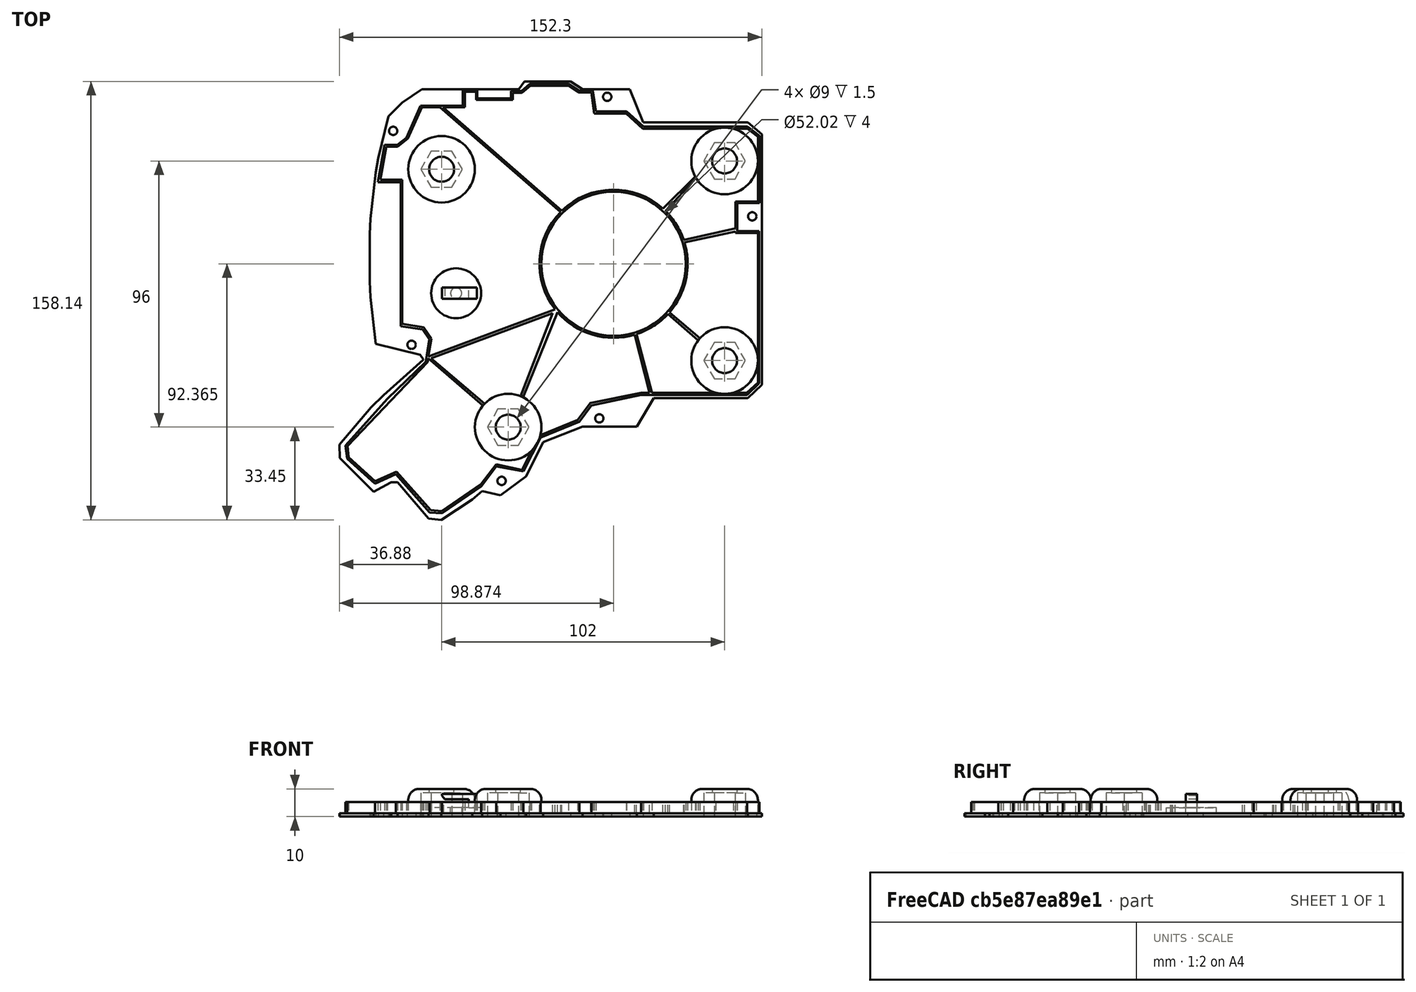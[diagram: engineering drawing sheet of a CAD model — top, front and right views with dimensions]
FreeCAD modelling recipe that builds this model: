
FCSTD DOCUMENT  (FreeCAD 0.19R19127 (Git))
Label: bottom
License: All rights reserved
LicenseURL: http://en.wikipedia.org/wiki/All_rights_reserved
objects: Part::Extrusion×13, Sketcher::SketchObject×9, Part::Cut×7, Part::MultiFuse×2, Mesh::Feature×1, Part::Fillet×1
note: 32 computed .brp shape members not serialized (recipe doc carries the construction recipe); baked Part::Feature solids carry a one-line shape summary decoded from their .brp

FEATURE [Mesh::Feature] Micro_push_button
  Placement = pos=(-31.692,-13.956,0) rot=(0,1,0;3.14159rad)
FEATURE [Sketcher::SketchObject] Sketch
  Placement = pos=(0,0,0) rot=(1,0,0;1.5708rad)
  sketch-geometry (7):
    g0: LineSegment StartX=-27.2326 StartY=-4.41101 StartZ=0 EndX=-27.2326 EndY=-1.0147 EndZ=0
    g1: LineSegment StartX=-27.2326 StartY=-1.0147 StartZ=0 EndX=-35.909 EndY=-1.0147 EndZ=0
    g2: LineSegment StartX=-35.909 StartY=-1.0147 StartZ=0 EndX=-36.8322 EndY=0.249898 EndZ=0
    g3: LineSegment StartX=-36.8322 StartY=0.249898 StartZ=0 EndX=-36.8322 EndY=0.921976 EndZ=0
    g4: LineSegment StartX=-36.8322 StartY=0.921976 StartZ=0 EndX=-24.2326 EndY=0.921976 EndZ=0
    g5: LineSegment StartX=-24.2326 StartY=0.921976 StartZ=0 EndX=-24.2326 EndY=-4.41101 EndZ=0
    g6: LineSegment StartX=-24.2326 StartY=-4.41101 StartZ=0 EndX=-27.2326 EndY=-4.41101 EndZ=0
  constraints (14):
    c: Vertical(g0)
    c: Coincident(g0,g1)
    c: Horizontal(g1)
    c: Coincident(g1,g2)
    c: Coincident(g2,g3)
    c: Vertical(g3)
    c: Coincident(g3,g4)
    c: Horizontal(g4)
    c: Coincident(g4,g5)
    c: Vertical(g5)
    c: Coincident(g6,g5)
    c: Coincident(g6,g0)
    c: Horizontal(g6)
    c: Distance(g6) = 3
FEATURE [Part::Extrusion] Extrude  label="Schalterhalter"
  Base = -> Sketch
  Dir = (0,-1,2e-16)
  DirMode = 2
  FaceMakerClass = Part::FaceMakerBullseye
  LengthFwd = 4
  LengthRev = 0
  Placement = pos=(0,-10.7,0) rot=(0,0,1;0rad)
  Solid = true
  Symmetric = false
FEATURE [Sketcher::SketchObject] Sketch031
  Placement = pos=(0,0,0) rot=(1,0,0;3.14159rad)
  sketch-geometry (93):
    g0: LineSegment StartX=-24.1385 StartY=-60.4779 StartZ=0 EndX=-29.3451 EndY=-60.4779 EndZ=0
    g1: LineSegment StartX=-29.3451 StartY=-60.4779 StartZ=0 EndX=-29.3451 EndY=-54.9411 EndZ=0
    g2: LineSegment StartX=-29.3451 StartY=-54.9411 StartZ=0 EndX=-44.617 EndY=-54.9411 EndZ=0
    g3: LineSegment StartX=-44.617 StartY=-54.9411 StartZ=0 EndX=-49.6427 EndY=-43.3137 EndZ=0
    g4: LineSegment StartX=-49.6427 StartY=-43.3137 StartZ=0 EndX=-52.9932 EndY=-40.8008 EndZ=0
    g5: LineSegment StartX=-52.9932 StartY=-40.8008 StartZ=0 EndX=-57.5179 EndY=-40.8008 EndZ=0
    g6: LineSegment StartX=-57.5179 StartY=-40.8008 StartZ=0 EndX=-59.9469 EndY=-27.3014 EndZ=0
    g7: LineSegment StartX=-59.9469 StartY=-27.3014 StartZ=0 EndX=-51.7705 EndY=-27.3014 EndZ=0
    g8: LineSegment StartX=-51.7705 StartY=-27.3014 StartZ=0 EndX=-51.7705 EndY=24.5767 EndZ=0
    g9: LineSegment StartX=-51.7705 StartY=24.5767 StartZ=0 EndX=-43.9004 EndY=25.7014 EndZ=0
    g10: LineSegment StartX=-43.9004 StartY=25.7014 StartZ=0 EndX=-41.4012 EndY=29.3252 EndZ=0
    g11: LineSegment StartX=-41.4012 StartY=29.3252 StartZ=0 EndX=-42.6508 EndY=37.4474 EndZ=0
    g12: LineSegment StartX=-42.6508 StartY=37.4474 StartZ=0 EndX=-56.5226 EndY=50.7262 EndZ=0
    g13: LineSegment StartX=-56.5226 StartY=50.7262 StartZ=0 EndX=-71.6425 EndY=67.7205 EndZ=0
    g14: LineSegment StartX=-71.6425 StartY=67.7205 StartZ=0 EndX=-71.0177 EndY=72.3439 EndZ=0
    g15: LineSegment StartX=-71.0177 StartY=72.3439 StartZ=0 EndX=-61.0211 EndY=81.3409 EndZ=0
    g16: LineSegment StartX=-61.0211 StartY=81.3409 StartZ=0 EndX=-53.5236 EndY=77.967 EndZ=0
    g17: LineSegment StartX=-53.5236 StartY=77.967 StartZ=0 EndX=-41.2663 EndY=91.7395 EndZ=0
    g18: LineSegment StartX=-41.2663 StartY=91.7395 StartZ=0 EndX=-36.8928 EndY=92.1144 EndZ=0
    g19: LineSegment StartX=-36.8928 StartY=92.1144 StartZ=0 EndX=-22.7725 EndY=82.3677 EndZ=0
    g20: LineSegment StartX=-22.7725 StartY=82.3677 StartZ=0 EndX=-17.2707 EndY=75.2106 EndZ=0
    g21: LineSegment StartX=-17.2707 StartY=75.2106 StartZ=0 EndX=-7.52765 EndY=76.9945 EndZ=0
    g22: LineSegment StartX=-7.52765 StartY=76.9945 StartZ=0 EndX=-1.25529 EndY=64.7175 EndZ=0
    g23: LineSegment StartX=-1.25529 StartY=64.7175 StartZ=0 EndX=12.6151 EndY=59.0944 EndZ=0
    g24: LineSegment StartX=12.6151 StartY=59.0944 StartZ=0 EndX=16.9593 EndY=53.2146 EndZ=0
    g25: LineSegment StartX=16.9593 StartY=53.2146 StartZ=0 EndX=34.8576 EndY=49.3476 EndZ=0
    g26: LineSegment StartX=34.8576 StartY=49.3476 StartZ=0 EndX=73.1246 EndY=49.3476 EndZ=0
    g27: LineSegment StartX=73.1246 StartY=49.3476 StartZ=0 EndX=77.4982 EndY=45.2021 EndZ=0
    g28: LineSegment StartX=77.4982 StartY=45.2021 StartZ=0 EndX=77.4982 EndY=-9.69727 EndZ=0
    g29: LineSegment StartX=77.4982 StartY=-9.69727 StartZ=0 EndX=69.5024 EndY=-9.69727 EndZ=0
    g30: LineSegment StartX=69.5024 StartY=-9.69727 StartZ=0 EndX=69.5024 EndY=-19.8189 EndZ=0
    g31: LineSegment StartX=69.5024 StartY=-19.8189 StartZ=0 EndX=77.6247 EndY=-19.8189 EndZ=0
    g32: LineSegment StartX=77.6247 StartY=-19.8189 StartZ=0 EndX=77.6247 EndY=-44.0607 EndZ=0
    g33: LineSegment StartX=77.6247 StartY=-44.0607 StartZ=0 EndX=73.2508 EndY=-47.3458 EndZ=0
    g34: LineSegment StartX=73.2508 StartY=-47.3458 StartZ=0 EndX=35.7634 EndY=-47.3458 EndZ=0
    g35: LineSegment StartX=35.7634 StartY=-47.3458 StartZ=0 EndX=29.7437 EndY=-52.8546 EndZ=0
    g36: LineSegment StartX=29.7437 StartY=-52.8546 StartZ=0 EndX=18.6224 EndY=-52.8546 EndZ=0
    g37: LineSegment StartX=18.6224 StartY=-52.8546 StartZ=0 EndX=17.5482 EndY=-60.3492 EndZ=0
    g38: LineSegment StartX=17.5482 StartY=-60.3492 StartZ=0 EndX=12.4995 EndY=-60.3492 EndZ=0
    g39: LineSegment StartX=12.4995 StartY=-60.3492 StartZ=0 EndX=8.72547 EndY=-62.7272 EndZ=0
    g40: LineSegment StartX=8.72547 StartY=-62.7272 StartZ=0 EndX=-5.26983 EndY=-62.7272 EndZ=0
    g41: LineSegment StartX=-5.26983 StartY=-62.7272 StartZ=0 EndX=-8.14386 EndY=-60.228 EndZ=0
    g42: LineSegment StartX=-8.14386 StartY=-60.228 StartZ=0 EndX=-12.0176 EndY=-60.228 EndZ=0
    g43: LineSegment StartX=-12.0176 StartY=-60.228 StartZ=0 EndX=-12.0176 EndY=-57.6039 EndZ=0
    g44: LineSegment StartX=-12.0176 StartY=-57.6039 StartZ=0 EndX=-24.1385 EndY=-57.6039 EndZ=0
    g45: LineSegment StartX=-24.1385 StartY=-57.6039 StartZ=0 EndX=-24.1385 EndY=-60.4779 EndZ=0
    g46: LineSegment StartX=16.9355 StartY=-59.7161 StartZ=0 EndX=12.3003 EndY=-59.7161 EndZ=0
    g47: LineSegment StartX=12.3003 StartY=-59.7161 StartZ=0 EndX=8.68721 EndY=-62.1852 EndZ=0
    g48: LineSegment StartX=8.68721 StartY=-62.1852 StartZ=0 EndX=-5.01254 EndY=-62.1852 EndZ=0
    g49: LineSegment StartX=-5.01254 StartY=-62.1852 StartZ=0 EndX=-8.06111 EndY=-59.5222 EndZ=0
    g50: LineSegment StartX=-8.06111 StartY=-59.5222 StartZ=0 EndX=-11.3675 EndY=-59.5222 EndZ=0
    g51: LineSegment StartX=-11.3675 StartY=-59.5222 StartZ=0 EndX=-11.3675 EndY=-57.1049 EndZ=0
    g52: LineSegment StartX=-11.3675 StartY=-57.1049 StartZ=0 EndX=-24.5978 EndY=-57.1049 EndZ=0
    g53: LineSegment StartX=-24.5978 StartY=-57.1049 StartZ=0 EndX=-24.5978 EndY=-59.9642 EndZ=0
    g54: LineSegment StartX=-24.5978 StartY=-59.9642 StartZ=0 EndX=-28.6249 EndY=-59.9642 EndZ=0
    g55: LineSegment StartX=-28.6249 StartY=-59.9642 StartZ=0 EndX=-28.6249 EndY=-54.4316 EndZ=0
    g56: LineSegment StartX=-28.6249 StartY=-54.4316 StartZ=0 EndX=-44.1423 EndY=-54.4316 EndZ=0
    g57: LineSegment StartX=-44.1423 StartY=-54.4316 StartZ=0 EndX=-49.115 EndY=-43.0922 EndZ=0
    g58: LineSegment StartX=-49.115 StartY=-43.0922 StartZ=0 EndX=-52.8786 EndY=-40.1566 EndZ=0
    g59: LineSegment StartX=-52.8786 StartY=-40.1566 StartZ=0 EndX=-56.8752 EndY=-40.1566 EndZ=0
    g60: LineSegment StartX=-56.8752 StartY=-40.1566 StartZ=0 EndX=-59.0956 EndY=-28.248 EndZ=0
    g61: LineSegment StartX=-59.0956 StartY=-28.248 StartZ=0 EndX=-51.2672 EndY=-28.248 EndZ=0
    g62: LineSegment StartX=-51.2672 StartY=-28.248 StartZ=0 EndX=-51.2672 EndY=23.7736 EndZ=0
    g63: LineSegment StartX=-51.2672 StartY=23.7736 StartZ=0 EndX=-43.511 EndY=24.9404 EndZ=0
    g64: LineSegment StartX=-43.511 StartY=24.9404 StartZ=0 EndX=-40.7191 EndY=29.0922 EndZ=0
    g65: LineSegment StartX=-40.7191 StartY=29.0922 StartZ=0 EndX=-42.0729 EndY=37.535 EndZ=0
    g66: LineSegment StartX=-42.0729 StartY=37.535 StartZ=0 EndX=-70.8807 EndY=67.743 EndZ=0
    g67: LineSegment StartX=-70.8807 StartY=67.743 StartZ=0 EndX=-70.5044 EndY=71.8077 EndZ=0
    g68: LineSegment StartX=-70.5044 StartY=71.8077 StartZ=0 EndX=-60.9793 EndY=80.5094 EndZ=0
    g69: LineSegment StartX=-60.9793 StartY=80.5094 StartZ=0 EndX=-53.2638 EndY=77.0092 EndZ=0
    g70: LineSegment StartX=-53.2638 StartY=77.0092 StartZ=0 EndX=-40.9455 EndY=90.9086 EndZ=0
    g71: LineSegment StartX=-40.9455 StartY=90.9086 StartZ=0 EndX=-37.0313 EndY=91.2473 EndZ=0
    g72: LineSegment StartX=-37.0313 StartY=91.2473 StartZ=0 EndX=-22.7567 EndY=81.4559 EndZ=0
    g73: LineSegment StartX=-22.7567 StartY=81.4559 StartZ=0 EndX=-17.3118 EndY=74.4294 EndZ=0
    g74: LineSegment StartX=-17.3118 StartY=74.4294 StartZ=0 EndX=-8.02792 EndY=76.4412 EndZ=0
    g75: LineSegment StartX=-8.02792 StartY=76.4412 StartZ=0 EndX=-1.89314 EndY=64.0587 EndZ=0
    g76: LineSegment StartX=-1.89314 StartY=64.0587 StartZ=0 EndX=12.006 EndY=58.4019 EndZ=0
    g77: LineSegment StartX=12.006 StartY=58.4019 StartZ=0 EndX=16.5662 EndY=52.3162 EndZ=0
    g78: LineSegment StartX=16.5662 StartY=52.3162 StartZ=0 EndX=34.9016 EndY=48.5664 EndZ=0
    g79: LineSegment StartX=34.9016 StartY=48.5664 StartZ=0 EndX=73.0125 EndY=48.5664 EndZ=0
    g80: LineSegment StartX=73.0125 StartY=48.5664 StartZ=0 EndX=77.0928 EndY=44.9063 EndZ=0
    g81: LineSegment StartX=77.0928 StartY=44.9063 StartZ=0 EndX=77.0928 EndY=-8.9817 EndZ=0
    g82: LineSegment StartX=77.0928 StartY=-8.9817 StartZ=0 EndX=68.9167 EndY=-8.9817 EndZ=0
    g83: LineSegment StartX=68.9167 StartY=-8.9817 StartZ=0 EndX=68.9167 EndY=-20.3983 EndZ=0
    g84: LineSegment StartX=68.9167 StartY=-20.3983 StartZ=0 EndX=77.0849 EndY=-20.3983 EndZ=0
    g85: LineSegment StartX=77.0849 StartY=-20.3983 StartZ=0 EndX=77.0849 EndY=-43.7447 EndZ=0
    g86: LineSegment StartX=77.0849 StartY=-43.7447 StartZ=0 EndX=73.2839 EndY=-46.5781 EndZ=0
    g87: LineSegment StartX=73.2839 StartY=-46.5781 StartZ=0 EndX=35.499 EndY=-46.5781 EndZ=0
    g88: LineSegment StartX=35.499 StartY=-46.5781 StartZ=0 EndX=29.59 EndY=-52.0327 EndZ=0
    g89: LineSegment StartX=29.59 StartY=-52.0327 StartZ=0 EndX=17.9893 EndY=-52.0327 EndZ=0
    g90: LineSegment StartX=17.9893 StartY=-52.0327 StartZ=0 EndX=16.9355 EndY=-59.7161 EndZ=0
    g91: Circle CenterX=24.994 CenterY=2.08531 CenterZ=0 NormalX=0 NormalY=0 NormalZ=1 AngleXU=0 Radius=26.0078
    g92: Circle CenterX=24.994 CenterY=2.08531 CenterZ=0 NormalX=0 NormalY=0 NormalZ=1 AngleXU=0 Radius=26.7002
  constraints (132):
    c: Horizontal(g0)
    c: Coincident(g0,g1)
    c: Vertical(g1)
    c: Coincident(g1,g2)
    c: Horizontal(g2)
    c: Coincident(g2,g3)
    c: Coincident(g3,g4)
    c: Coincident(g4,g5)
    c: Horizontal(g5)
    c: Coincident(g5,g6)
    c: Coincident(g6,g7)
    c: Horizontal(g7)
    c: Coincident(g7,g8)
    c: Vertical(g8)
    c: Coincident(g8,g9)
    c: Coincident(g9,g10)
    c: Coincident(g10,g11)
    c: Coincident(g11,g12)
    c: Coincident(g12,g13)
    c: Coincident(g13,g14)
    c: Coincident(g14,g15)
    c: Coincident(g15,g16)
    c: Coincident(g16,g17)
    c: Coincident(g17,g18)
    c: Coincident(g18,g19)
    c: Coincident(g19,g20)
    c: Coincident(g20,g21)
    c: Coincident(g21,g22)
    c: Coincident(g22,g23)
    c: Coincident(g23,g24)
    c: Coincident(g24,g25)
    c: Coincident(g25,g26)
    c: Horizontal(g26)
    c: Coincident(g26,g27)
    c: Coincident(g27,g28)
    c: Vertical(g28)
    c: Coincident(g28,g29)
    c: Horizontal(g29)
    c: Coincident(g29,g30)
    c: Vertical(g30)
    c: Coincident(g30,g31)
    c: Horizontal(g31)
    c: Coincident(g31,g32)
    c: Vertical(g32)
    c: Coincident(g32,g33)
    c: Coincident(g33,g34)
    c: Horizontal(g34)
    c: Coincident(g34,g35)
    c: Coincident(g35,g36)
    c: Horizontal(g36)
    c: Coincident(g36,g37)
    c: Coincident(g37,g38)
    c: Horizontal(g38)
    c: Coincident(g38,g39)
    c: Coincident(g39,g40)
    c: Horizontal(g40)
    c: Coincident(g40,g41)
    c: Coincident(g41,g42)
    c: Horizontal(g42)
    c: Coincident(g42,g43)
    c: Vertical(g43)
    c: Coincident(g43,g44)
    c: Horizontal(g44)
    c: Coincident(g44,g45)
    c: Coincident(g45,g0)
    c: Vertical(g45)
    c: Horizontal(g46)
    c: Coincident(g46,g47)
    c: Coincident(g47,g48)
    c: Horizontal(g48)
    c: Coincident(g48,g49)
    c: Coincident(g49,g50)
    c: Horizontal(g50)
    c: Coincident(g50,g51)
    c: Vertical(g51)
    c: Coincident(g51,g52)
    c: Horizontal(g52)
    c: Coincident(g52,g53)
    c: Vertical(g53)
    c: Coincident(g53,g54)
    c: Horizontal(g54)
    c: Coincident(g54,g55)
    c: Vertical(g55)
    c: Coincident(g55,g56)
    c: Horizontal(g56)
    c: Coincident(g56,g57)
    c: Coincident(g57,g58)
    c: Coincident(g58,g59)
    c: Horizontal(g59)
    c: Coincident(g59,g60)
    c: Coincident(g60,g61)
    c: Horizontal(g61)
    c: Coincident(g61,g62)
    c: Vertical(g62)
    c: Coincident(g62,g63)
    c: Coincident(g63,g64)
    c: Coincident(g64,g65)
    c: Coincident(g65,g66)
    c: Coincident(g66,g67)
    c: Coincident(g67,g68)
    c: Coincident(g68,g69)
    c: Coincident(g69,g70)
    c: Coincident(g70,g71)
    c: Coincident(g71,g72)
    c: Coincident(g72,g73)
    c: Coincident(g73,g74)
    c: Coincident(g74,g75)
    c: Coincident(g75,g76)
    c: Coincident(g76,g77)
    c: Coincident(g77,g78)
    c: Coincident(g78,g79)
    c: Horizontal(g79)
    c: Coincident(g79,g80)
    c: Coincident(g80,g81)
    c: Vertical(g81)
    c: Coincident(g81,g82)
    c: Horizontal(g82)
    c: Coincident(g82,g83)
    c: Vertical(g83)
    c: Coincident(g83,g84)
    c: Horizontal(g84)
    c: Coincident(g84,g85)
    c: Vertical(g85)
    c: Coincident(g85,g86)
    c: Coincident(g86,g87)
    c: Horizontal(g87)
    c: Coincident(g87,g88)
    c: Coincident(g88,g89)
    c: Horizontal(g89)
    c: Coincident(g89,g90)
    c: Coincident(g90,g46)
    c: Coincident(g92,g91)
FEATURE [Part::Extrusion] Extrude026
  Base = -> Sketch031
  Dir = (0,0,-1)
  DirMode = 2
  FaceMakerClass = Part::FaceMakerBullseye
  LengthFwd = 4
  LengthRev = 0
  Placement = pos=(0,0,-2) rot=(0,0,1;0rad)
  Solid = true
  Symmetric = false
FEATURE [Sketcher::SketchObject] Sketch032
  sketch-geometry (31):
    g0: LineSegment StartX=-41.9443 StartY=-35.5996 StartZ=0 EndX=4.06286 EndY=-18.4644 EndZ=0
    g1: LineSegment StartX=4.06286 StartY=-18.4644 StartZ=0 EndX=4.79359 EndY=-19.3738 EndZ=0
    g2: LineSegment StartX=-41.9819 StartY=-36.1265 StartZ=0 EndX=-41.9443 EndY=-35.5996 EndZ=0
    g3: LineSegment StartX=32.5107 StartY=-27.5505 StartZ=0 EndX=38.0602 EndY=-48.9351 EndZ=0
    g4: LineSegment StartX=38.0602 StartY=-48.9351 StartZ=0 EndX=38.8414 EndY=-48.8117 EndZ=0
    g5: LineSegment StartX=38.8414 StartY=-48.8117 StartZ=0 EndX=33.2508 EndY=-27.3038 EndZ=0
    g6: LineSegment StartX=33.2508 StartY=-27.3038 StartZ=0 EndX=32.5107 EndY=-27.5505 EndZ=0
    g7: LineSegment StartX=50.4075 StartY=5.61281 StartZ=0 EndX=69.1512 EndY=9.61147 EndZ=0
    g8: LineSegment StartX=69.1512 StartY=9.61147 StartZ=0 EndX=69.1512 EndY=10.7361 EndZ=0
    g9: LineSegment StartX=69.1512 StartY=10.7361 StartZ=0 EndX=49.9077 EndY=6.36256 EndZ=0
    g10: LineSegment StartX=49.9077 StartY=6.36256 StartZ=0 EndX=50.4075 EndY=5.61281 EndZ=0
    g11: LineSegment StartX=6.62474 StartY=16.8187 StartZ=0 EndX=-36.2283 EndY=54.1389 EndZ=0
    g12: LineSegment StartX=-36.2283 StartY=54.1389 StartZ=0 EndX=-36.7246 EndY=54.6574 EndZ=0
    g13: LineSegment StartX=-36.7246 StartY=54.6574 StartZ=0 EndX=-37.7589 EndY=54.5817 EndZ=0
    g14: LineSegment StartX=-37.7589 StartY=54.5817 StartZ=0 EndX=6.17556 EndY=16.3134 EndZ=0
    g15: LineSegment StartX=6.17556 StartY=16.3134 StartZ=0 EndX=6.62474 EndY=16.8187 EndZ=0
    g16: LineSegment StartX=-41.9819 StartY=-36.1265 StartZ=0 EndX=-21.3967 EndY=-53.897 EndZ=0
    g17: LineSegment StartX=-20.9317 StartY=-52.9671 StartZ=0 EndX=-40.8089 EndY=-36.1703 EndZ=0
    g18: LineSegment StartX=-20.9317 StartY=-52.9671 StartZ=0 EndX=-21.3967 EndY=-53.897 EndZ=0
    g19: LineSegment StartX=-40.8089 StartY=-36.1703 StartZ=0 EndX=3.04998 EndY=-19.955 EndZ=0
    g20: LineSegment StartX=3.04998 StartY=-19.955 StartZ=0 EndX=-8.80659 EndY=-50.4682 EndZ=0
    g21: LineSegment StartX=-8.80659 StartY=-50.4682 StartZ=0 EndX=-7.81854 EndY=-50.817 EndZ=0
    g22: LineSegment StartX=-7.81854 StartY=-50.817 StartZ=0 EndX=4.79359 EndY=-19.3738 EndZ=0
    g23: LineSegment StartX=44.4369 StartY=-20.0606 StartZ=0 EndX=56.2289 EndY=-30.3786 EndZ=0
    g24: LineSegment StartX=56.2289 StartY=-30.3786 StartZ=0 EndX=56.8358 EndY=-29.5982 EndZ=0
    g25: LineSegment StartX=56.8358 StartY=-29.5982 StartZ=0 EndX=45.0439 EndY=-19.5404 EndZ=0
    g26: LineSegment StartX=45.0439 StartY=-19.5404 StartZ=0 EndX=44.4369 EndY=-20.0606 EndZ=0
    g27: LineSegment StartX=55.0145 StartY=29.918 StartZ=0 EndX=42.7023 EndY=17.6926 EndZ=0
    g28: LineSegment StartX=42.7023 StartY=17.6926 StartZ=0 EndX=43.396 EndY=16.6521 EndZ=0
    g29: LineSegment StartX=43.396 StartY=16.6521 StartZ=0 EndX=55.5348 EndY=29.6579 EndZ=0
    g30: LineSegment StartX=55.5348 StartY=29.6579 StartZ=0 EndX=55.0145 EndY=29.918 EndZ=0
  constraints (32):
    c: Coincident(g0,g1)
    c: Coincident(g2,g0)
    c: Coincident(g3,g4)
    c: Coincident(g4,g5)
    c: Coincident(g5,g6)
    c: Coincident(g6,g3)
    c: Coincident(g7,g8)
    c: Vertical(g8)
    c: Coincident(g8,g9)
    c: Coincident(g9,g10)
    c: Coincident(g10,g7)
    c: Coincident(g11,g12)
    c: Coincident(g12,g13)
    c: Coincident(g13,g14)
    c: Coincident(g14,g15)
    c: Coincident(g15,g11)
    c: Coincident(g16,g2)
    c: Coincident(g18,g17)
    c: Coincident(g18,g16)
    c: Coincident(g17,g19)
    c: Coincident(g19,g20)
    c: Coincident(g20,g21)
    c: Coincident(g21,g22)
    c: Coincident(g22,g1)
    c: Coincident(g23,g24)
    c: Coincident(g24,g25)
    c: Coincident(g25,g26)
    c: Coincident(g26,g23)
    c: Coincident(g27,g28)
    c: Coincident(g28,g29)
    c: Coincident(g29,g30)
    c: Coincident(g30,g27)
FEATURE [Part::Extrusion] Extrude028  label="Querstreben"
  Base = -> Sketch032
  Dir = (0,0,1)
  DirMode = 2
  FaceMakerClass = Part::FaceMakerBullseye
  LengthFwd = 4
  LengthRev = 0
  Placement = pos=(0,0,-6) rot=(0,0,1;0rad)
  Solid = true
  Symmetric = false
FEATURE [Sketcher::SketchObject] Sketch054
  Placement = pos=(0,0,-4) rot=(1,0,0;3.14159rad)
  sketch-geometry (41):
    g0: LineSegment StartX=-44.1096 StartY=-60.8699 StartZ=0 EndX=-51.1597 EndY=-56.0764 EndZ=0
    g1: LineSegment StartX=-51.1597 StartY=-56.0764 StartZ=0 EndX=-56.1597 EndY=-51.0764 EndZ=0
    g2: LineSegment StartX=-56.1597 StartY=-51.0764 StartZ=0 EndX=-59.8373 EndY=-36.0023 EndZ=0
    g3: LineSegment StartX=-59.8373 StartY=-36.0023 StartZ=0 EndX=-60.7273 EndY=-30.9176 EndZ=0
    g4: LineSegment StartX=-60.7273 StartY=-30.9176 StartZ=0 EndX=-62.6338 EndY=-14.0857 EndZ=0
    g5: LineSegment StartX=-62.6338 StartY=-14.0857 StartZ=0 EndX=-62.9339 EndY=-8.65493 EndZ=0
    g6: LineSegment StartX=-62.9339 StartY=-8.65493 StartZ=0 EndX=-62.9339 EndY=8.50371 EndZ=0
    g7: LineSegment StartX=-62.9339 StartY=8.50371 StartZ=0 EndX=-62.6306 EndY=14.1113 EndZ=0
    g8: LineSegment StartX=-62.6306 StartY=14.1113 StartZ=0 EndX=-60.7274 EndY=30.9184 EndZ=0
    g9: LineSegment StartX=-60.7274 StartY=30.9184 StartZ=0 EndX=-44.7719 EndY=34.9058 EndZ=0
    g10: LineSegment StartX=-44.7719 StartY=34.9058 StartZ=0 EndX=-43.644 EndY=36.5944 EndZ=0
    g11: LineSegment StartX=-57.9733 StartY=49.5001 StartZ=0 EndX=-62.4016 EndY=53.8882 EndZ=0
    g12: LineSegment StartX=-62.4016 StartY=53.8882 StartZ=0 EndX=-73.8841 EndY=67.2952 EndZ=0
    g13: LineSegment StartX=-73.8841 StartY=67.2952 StartZ=0 EndX=-73.728 EndY=72.1099 EndZ=0
    g14: LineSegment StartX=-73.728 StartY=72.1099 StartZ=0 EndX=-61.4812 EndY=84.3202 EndZ=0
    g15: LineSegment StartX=-61.4812 StartY=84.3202 StartZ=0 EndX=-55.4564 EndY=80.9755 EndZ=0
    g16: LineSegment StartX=-52.9032 StartY=80.8654 StartZ=0 EndX=-41.6311 EndY=94.0008 EndZ=0
    g17: LineSegment StartX=-41.6311 StartY=94.0008 StartZ=0 EndX=-37.1205 EndY=94.4533 EndZ=0
    g18: LineSegment StartX=-22.3813 StartY=84.0862 StartZ=0 EndX=-15.8423 EndY=85.5184 EndZ=0
    g19: LineSegment StartX=-15.8423 StartY=85.5184 StartZ=0 EndX=-6.48612 EndY=78.7207 EndZ=0
    g20: LineSegment StartX=-6.48612 StartY=78.7207 StartZ=0 EndX=-0.423905 EndY=66.4387 EndZ=0
    g21: LineSegment StartX=-0.423905 StartY=66.4387 StartZ=0 EndX=13.8377 EndY=60.8699 EndZ=0
    g22: LineSegment StartX=13.8377 StartY=60.8699 StartZ=0 EndX=33.3369 EndY=60.8699 EndZ=0
    g23: LineSegment StartX=33.3369 StartY=60.8699 StartZ=0 EndX=39.4269 EndY=50.5485 EndZ=0
    g24: LineSegment StartX=39.4269 StartY=50.5485 StartZ=0 EndX=73.4211 EndY=50.5485 EndZ=0
    g25: LineSegment StartX=73.4211 StartY=50.5485 StartZ=0 EndX=78.4211 EndY=45.7188 EndZ=0
    g26: LineSegment StartX=78.4211 StartY=45.7188 StartZ=0 EndX=78.4211 EndY=-44.5398 EndZ=0
    g27: LineSegment StartX=78.4211 StartY=-44.5398 StartZ=0 EndX=73.4211 EndY=-48.8699 EndZ=0
    g28: LineSegment StartX=73.4211 StartY=-48.8699 StartZ=0 EndX=35.5981 EndY=-48.8699 EndZ=0
    g29: LineSegment StartX=35.5981 StartY=-48.8699 StartZ=0 EndX=30.8749 EndY=-60.8699 EndZ=0
    g30: LineSegment StartX=30.8749 StartY=-60.8699 StartZ=0 EndX=13.8377 EndY=-60.8699 EndZ=0
    g31: LineSegment StartX=13.8377 StartY=-60.8699 StartZ=0 EndX=9.45978 EndY=-63.6899 EndZ=0
    g32: LineSegment StartX=9.45978 StartY=-63.6899 StartZ=0 EndX=-7.15413 EndY=-63.6899 EndZ=0
    g33: LineSegment StartX=-7.15413 StartY=-63.6899 StartZ=0 EndX=-9.13059 EndY=-60.8699 EndZ=0
    g34: LineSegment StartX=-9.13059 StartY=-60.8699 StartZ=0 EndX=-44.1096 EndY=-60.8699 EndZ=0
    g35: LineSegment StartX=-43.644 StartY=36.5944 StartZ=0 EndX=-43.6091 EndY=36.688 EndZ=0
    g36: LineSegment StartX=-43.6091 StartY=36.688 StartZ=0 EndX=-57.9733 EndY=49.5001 EndZ=0
    g37: LineSegment StartX=-55.4564 StartY=80.9755 StartZ=0 EndX=-55.2037 EndY=80.9386 EndZ=0
    g38: LineSegment StartX=-55.2037 StartY=80.9386 StartZ=0 EndX=-52.9032 EndY=80.8654 EndZ=0
    g39: LineSegment StartX=-37.1205 StartY=94.4533 StartZ=0 EndX=-25.9498 EndY=87.0805 EndZ=0
    g40: LineSegment StartX=-25.9498 StartY=87.0805 StartZ=0 EndX=-22.3813 EndY=84.0862 EndZ=0
  constraints (49):
    c: Coincident(g0,g1)
    c: Coincident(g1,g2)
    c: Coincident(g2,g3)
    c: Coincident(g3,g4)
    c: Coincident(g4,g5)
    c: Coincident(g5,g6)
    c: Vertical(g6)
    c: Coincident(g6,g7)
    c: Coincident(g7,g8)
    c: Coincident(g8,g9)
    c: Coincident(g9,g10)
    c: Coincident(g11,g12)
    c: Coincident(g12,g13)
    c: Coincident(g13,g14)
    c: Coincident(g14,g15)
    c: Coincident(g16,g17)
    c: Coincident(g18,g19)
    c: Coincident(g19,g20)
    c: Coincident(g20,g21)
    c: Coincident(g21,g22)
    c: Horizontal(g22)
    c: Coincident(g22,g23)
    c: Coincident(g23,g24)
    c: Horizontal(g24)
    c: Coincident(g24,g25)
    c: Coincident(g25,g26)
    c: Vertical(g26)
    c: Coincident(g26,g27)
    c: Coincident(g27,g28)
    c: Horizontal(g28)
    c: Coincident(g28,g29)
    c: Coincident(g29,g30)
    c: Horizontal(g30)
    c: Coincident(g30,g31)
    c: Coincident(g31,g32)
    c: Horizontal(g32)
    c: Coincident(g32,g33)
    c: Coincident(g33,g34)
    c: Horizontal(g34)
    c: Coincident(g0,g34)
    c: Coincident(g35,g10)
    c: Coincident(g36,g35)
    c: Coincident(g36,g11)
    c: Coincident(g37,g15)
    c: Coincident(g38,g37)
    c: Coincident(g38,g16)
    c: Coincident(g39,g17)
    c: Coincident(g40,g39)
    c: Coincident(g40,g18)
FEATURE [Part::Extrusion] Extrude044  label="Grund"
  Base = -> Sketch054
  Dir = (0,0,-1)
  DirMode = 2
  FaceMakerClass = Part::FaceMakerBullseye
  LengthFwd = 1.25
  LengthRev = 0
  Placement = pos=(0,0,-2) rot=(0,0,1;0rad)
  Solid = true
  Symmetric = false
FEATURE [Sketcher::SketchObject] Sketch002
  sketch-geometry (7):
    g0: LineSegment StartX=3.75278 StartY=6.5 StartZ=0 EndX=-3.75278 EndY=6.5 EndZ=0
    g1: LineSegment StartX=-3.75278 StartY=6.5 StartZ=0 EndX=-7.50555 EndY=-1.2284e-12 EndZ=0
    g2: LineSegment StartX=-7.50555 StartY=-1.2284e-12 StartZ=0 EndX=-3.75278 EndY=-6.5 EndZ=0
    g3: LineSegment StartX=-3.75278 StartY=-6.5 StartZ=0 EndX=3.75278 EndY=-6.5 EndZ=0
    g4: LineSegment StartX=3.75278 StartY=-6.5 StartZ=0 EndX=7.50555 EndY=6.422e-13 EndZ=0
    g5: LineSegment StartX=7.50555 StartY=6.419e-13 StartZ=0 EndX=3.75278 EndY=6.5 EndZ=0
    g6: Circle [constr] CenterX=0 CenterY=0 CenterZ=0 NormalX=0 NormalY=0 NormalZ=1 AngleXU=0 Radius=7.50555
  constraints (16):
    c: Coincident(g0,g1)
    c: Coincident(g1,g2)
    c: Coincident(g2,g3)
    c: Coincident(g3,g4)
    c: Coincident(g4,g5)
    c: Coincident(g5,g0)
    c: Equal(g0, g1-g5) x5
    c: PointOnObject(g0,g6)
    c: PointOnObject(g1,g6)
    c: PointOnObject(g2,g6)
    c: PointOnObject(g3,g6)
    c: PointOnObject(g4,g6)
    c: PointOnObject(g5,g6)
    c: Horizontal(g0)
    c: Distance(g3,g1) = 13
    c: Coincident(g6,g-1)
FEATURE [Part::Extrusion] Extrude002  label="Mutterloch"
  Base = -> Sketch002
  Dir = (0,0,1)
  DirMode = 2
  FaceMakerClass = Part::FaceMakerBullseye
  LengthFwd = 8.5
  LengthRev = 0
  Reversed = true
  Solid = true
  Symmetric = false
FEATURE [Sketcher::SketchObject] Sketch055
  sketch-geometry (1):
    g0: Circle CenterX=0 CenterY=0 CenterZ=0 NormalX=0 NormalY=0 NormalZ=1 AngleXU=0 Radius=12
  constraints (2):
    c: Coincident(g0,g-1)
    c: Radius(g0) = 12
FEATURE [Part::Extrusion] Extrude045
  Base = -> Sketch055
  Dir = (0,0,1)
  DirMode = 2
  FaceMakerClass = Part::FaceMakerBullseye
  LengthFwd = 10
  LengthRev = 0
  Placement = pos=(0,0,-8.5) rot=(0,0,1;0rad)
  Solid = true
  Symmetric = false
FEATURE [Part::Fillet] Fillet
  Base = -> Extrude045
  Edges = 1 edges r=4: [Edge3]
FEATURE [Sketcher::SketchObject] Sketch056
  sketch-geometry (1):
    g0: Circle CenterX=0 CenterY=0 CenterZ=0 NormalX=0 NormalY=0 NormalZ=1 AngleXU=0 Radius=4.5
  constraints (2):
    c: Coincident(g0,g-1)
    c: Radius(g0) = 4.5
FEATURE [Part::Extrusion] Extrude046
  Base = -> Sketch056
  Dir = (0,0,1)
  DirMode = 2
  FaceMakerClass = Part::FaceMakerBullseye
  LengthFwd = 10
  LengthRev = 0
  Solid = true
  Symmetric = false
FEATURE [Part::Cut] Cut
  Base = -> Fillet
  Tool = -> Extrude046
FEATURE [Part::Cut] Cut001
  Base = -> Cut
  Placement = pos=(65,-37,1.25) rot=(0,0,1;0rad)
  Tool = -> Extrude002
FEATURE [Part::Cut] Cut002
  Base = -> Cut
  Placement = pos=(65,35,1.25) rot=(0,0,1;0rad)
  Tool = -> Extrude002
FEATURE [Part::Cut] Cut003
  Base = -> Cut
  Placement = pos=(-37,32,1.25) rot=(0,0,1;0rad)
  Tool = -> Extrude002
FEATURE [Part::Cut] Cut004
  Base = -> Cut
  Placement = pos=(-13,-61,1.25) rot=(0,0,1;0rad)
  Tool = -> Extrude002
FEATURE [Part::Extrusion] Extrude047  label="Mutterloch001"
  Base = -> Sketch002
  Dir = (0,0,1)
  DirMode = 2
  FaceMakerClass = Part::FaceMakerBullseye
  LengthFwd = 8.5
  LengthRev = 0
  Placement = pos=(65,-37,1.25) rot=(0,0,1;0rad)
  Reversed = true
  Solid = true
  Symmetric = false
FEATURE [Part::Extrusion] Extrude048  label="Mutterloch002"
  Base = -> Sketch002
  Dir = (0,0,1)
  DirMode = 2
  FaceMakerClass = Part::FaceMakerBullseye
  LengthFwd = 8.5
  LengthRev = 0
  Placement = pos=(65,35,1.25) rot=(0,0,1;0rad)
  Reversed = true
  Solid = true
  Symmetric = false
FEATURE [Part::Extrusion] Extrude049  label="Mutterloch003"
  Base = -> Sketch002
  Dir = (0,0,1)
  DirMode = 2
  FaceMakerClass = Part::FaceMakerBullseye
  LengthFwd = 8.5
  LengthRev = 0
  Placement = pos=(-37,32,1.25) rot=(0,0,1;0rad)
  Reversed = true
  Solid = true
  Symmetric = false
FEATURE [Part::Extrusion] Extrude050  label="Mutterloch004"
  Base = -> Sketch002
  Dir = (0,0,1)
  DirMode = 2
  FaceMakerClass = Part::FaceMakerBullseye
  LengthFwd = 8.5
  LengthRev = 0
  Placement = pos=(-13,-61,1.25) rot=(0,0,1;0rad)
  Reversed = true
  Solid = true
  Symmetric = false
FEATURE [Part::MultiFuse] Fusion001
  Shapes = -> [Extrude050,Extrude049,Extrude048,Extrude047]
FEATURE [Part::Cut] Cut005
  Base = -> Extrude044
  Tool = -> Fusion001
FEATURE [Sketcher::SketchObject] Sketch033
  Placement = pos=(0,0,0) rot=(1,0,0;3.14159rad)
  sketch-geometry (2):
    g0: Circle CenterX=-31.7644 CenterY=12.7082 CenterZ=0 NormalX=0 NormalY=0 NormalZ=1 AngleXU=0 Radius=2
    g1: Circle CenterX=-31.7644 CenterY=12.7082 CenterZ=0 NormalX=0 NormalY=0 NormalZ=1 AngleXU=0 Radius=9
  constraints (3):
    c: Coincident(g1,g0)
    c: Radius(g0) = 2
    c: Radius(g1) = 9
FEATURE [Part::Extrusion] Extrude029  label="Schalterbasis"
  Base = -> Sketch033
  Dir = (0,0,-1)
  DirMode = 2
  FaceMakerClass = Part::FaceMakerBullseye
  LengthFwd = 2
  LengthRev = 0
  Placement = pos=(0,0,-4) rot=(0,0,1;0rad)
  Solid = true
  Symmetric = false
FEATURE [Sketcher::SketchObject] Sketch057
  Placement = pos=(0,0,0) rot=(1,0,0;3.14159rad)
  sketch-geometry (12):
    g0: Circle CenterX=-47.8116 CenterY=31.3188 CenterZ=0 NormalX=0 NormalY=0 NormalZ=1 AngleXU=0 Radius=1.5
    g1: Circle [constr] CenterX=-47.8116 CenterY=31.3188 CenterZ=0 NormalX=0 NormalY=0 NormalZ=1 AngleXU=0 Radius=2.64
    g2: Circle CenterX=-15.379 CenterY=80.3782 CenterZ=0 NormalX=0 NormalY=0 NormalZ=1 AngleXU=0 Radius=1.5
    g3: Circle [constr] CenterX=-15.379 CenterY=80.3782 CenterZ=0 NormalX=0 NormalY=0 NormalZ=1 AngleXU=0 Radius=2.64
    g4: Circle CenterX=19.8371 CenterY=57.8529 CenterZ=0 NormalX=0 NormalY=0 NormalZ=1 AngleXU=0 Radius=1.5
    g5: Circle [constr] CenterX=19.8371 CenterY=57.8529 CenterZ=0 NormalX=0 NormalY=0 NormalZ=1 AngleXU=0 Radius=2.64
    g6: Circle CenterX=74.9864 CenterY=-15.0107 CenterZ=0 NormalX=0 NormalY=0 NormalZ=1 AngleXU=0 Radius=1.5
    g7: Circle [constr] CenterX=74.9864 CenterY=-15.0107 CenterZ=0 NormalX=0 NormalY=0 NormalZ=1 AngleXU=0 Radius=2.64
    g8: Circle CenterX=22.6987 CenterY=-58.1327 CenterZ=0 NormalX=0 NormalY=0 NormalZ=1 AngleXU=0 Radius=1.5
    g9: Circle [constr] CenterX=22.6987 CenterY=-58.1327 CenterZ=0 NormalX=0 NormalY=0 NormalZ=1 AngleXU=0 Radius=2.64
    g10: Circle CenterX=-54.4678 CenterY=-45.841 CenterZ=0 NormalX=0 NormalY=0 NormalZ=1 AngleXU=0 Radius=1.5
    g11: Circle [constr] CenterX=-54.4678 CenterY=-45.841 CenterZ=0 NormalX=0 NormalY=0 NormalZ=1 AngleXU=0 Radius=2.64
  constraints (10):
    c: Radius(g0) = 1.5
    c: Coincident(g1,g0)
    c: Radius(g1) = 2.64
    c: Equal(g0,g2) = 1.5
    c: Coincident(g3,g2)
    c: Equal(g1,g3) = 2.64
    c: Coincident(g5,g4)
    c: Coincident(g7,g6)
    c: Coincident(g9,g8)
    c: Coincident(g11,g10)
FEATURE [Part::Extrusion] Extrude051
  Base = -> Sketch057
  Dir = (0,0,-1)
  DirMode = 2
  FaceMakerClass = Part::FaceMakerBullseye
  LengthFwd = 2
  LengthRev = 0
  Placement = pos=(0,0,-6) rot=(0,0,1;0rad)
  Solid = true
  Symmetric = false
FEATURE [Part::Cut] Cut006
  Base = -> Cut005
  Tool = -> Extrude051
FEATURE [Part::MultiFuse] Fusion
  Shapes = -> [Extrude,Extrude026,Extrude028,Cut001,Cut002,Cut003,Cut004,Extrude029,Cut006]
